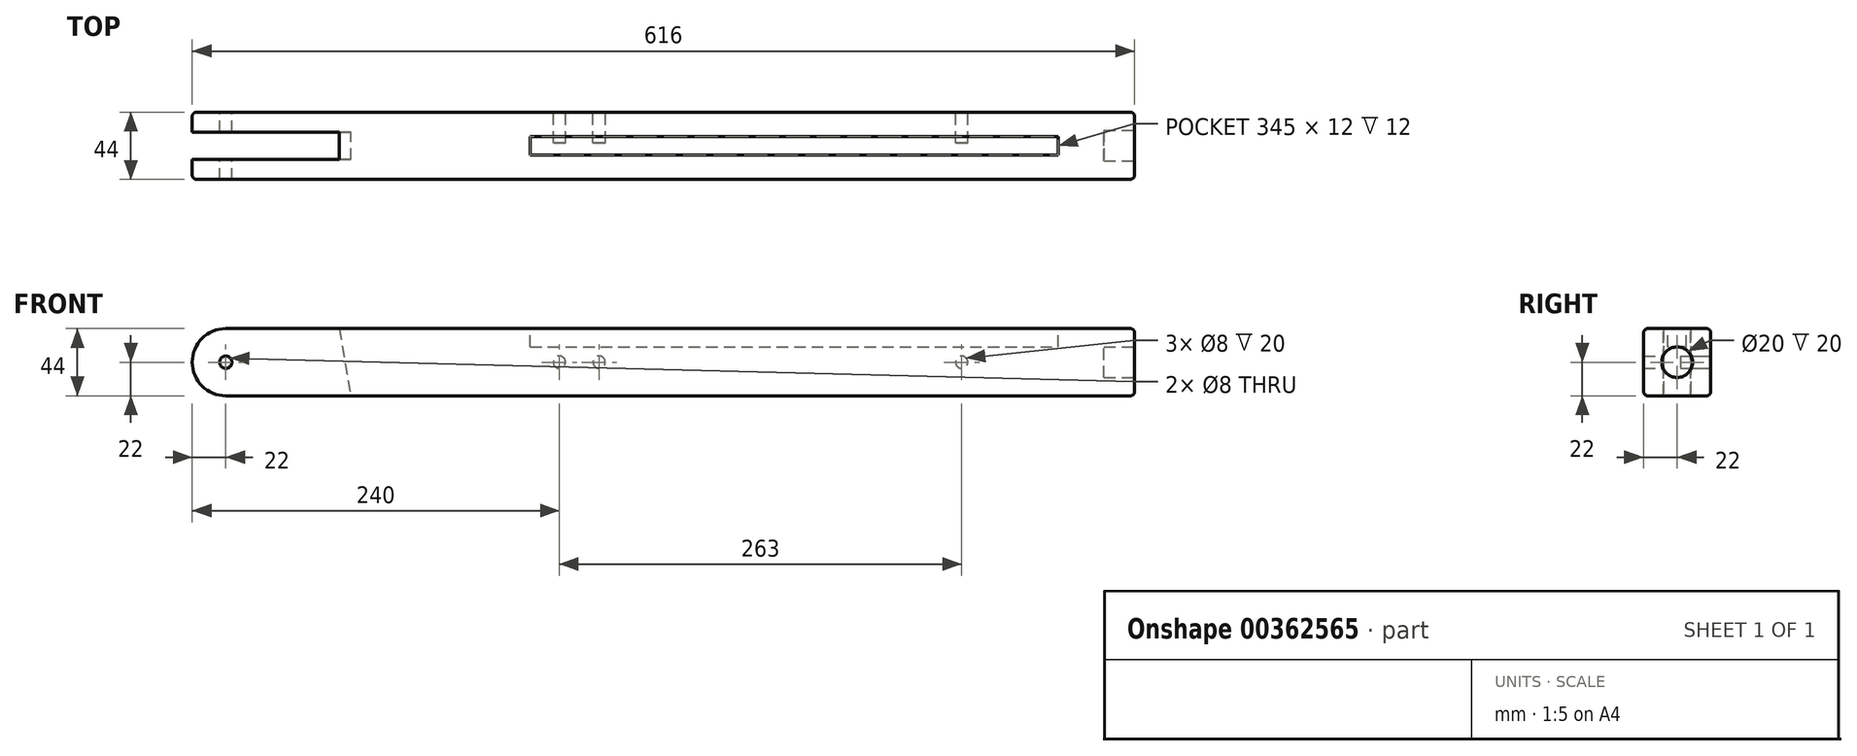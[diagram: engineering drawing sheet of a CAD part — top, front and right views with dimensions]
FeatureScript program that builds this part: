
annotation { "Feature Type Name" : "Feature", "Feature Type Description" : "" }
export const myFeature = defineFeature(function(context is Context, id is Id, definition is map)
    precondition{}
    {
        {
            var Q0;
            Q0=qCreatedBy(makeId("Front.planeOp"),FACE);
            var sketch = newSketch(context, id + "F0", { "sketchPlane" : qUnion([Q0])});
            skArc(sketch, "E0", {"start": v(0, 822) * mm, "mid": v(-22, 800) * mm, "end": v(0, 778) * mm});
            skLineSegment(sketch, "E1", {"start": v(0, 800) * mm, "end": v(594, 800) * mm, "construction": true});
            skLineSegment(sketch, "E2", {"start": v(0, 822) * mm, "end": v(594, 822) * mm});
            skLineSegment(sketch, "E3", {"start": v(594, 778) * mm, "end": v(0, 778) * mm});
            skLineSegment(sketch, "E4", {"start": v(594, 822) * mm, "end": v(594, 778) * mm});
            skLineSegment(sketch, "E5", {"start": v(0, 800) * mm, "end": v(-22, 800) * mm, "construction": true});
            skSolve(sketch);
        }
        {
            var Q0;
            Q0=makeQuery(id+"F0.imprint","IMPRINT",FACE,{"disambiguationData":[TD([[makeQuery(id+"F0.imprint","IMPRINT",EDGE,{"derivedFrom":sQuery(id+"F0.wireOp",EDGE,"E0")}),1.0]])]});
            extrude(context, id + "F1", {"entities" : qUnion([Q0]), "depth" : 44 * mm});
        }
        {
            var Q0;
            Q0=makeQuery(id+"F1.opExtrude","CAP_FACE",FACE,{"disambiguationData":[OSD([sQuery(id+"F0.wireOp",EDGE,"E0"),sQuery(id+"F0.wireOp",EDGE,"E2"),sQuery(id+"F0.wireOp",EDGE,"E3"),sQuery(id+"F0.wireOp",EDGE,"E4")])],"isStart":true});
            cPlane(context, id + "F2", {"entities" : qUnion([Q0]), "cplaneType" : CPlaneType.OFFSET, "offset" : 13 * mm, "oppositeDirection" : true, "width" : 150 * mm, "height" : 150 * mm});
        }
        {
            var Q0;
            Q0=qCreatedBy(id+"F2.planeOp",FACE);
            var sketch = newSketch(context, id + "F3", { "sketchPlane" : qUnion([Q0])});
            skLineSegment(sketch, "E6", {"start": v(22, 778) * mm, "end": v(22, 822) * mm});
            skLineSegment(sketch, "E7", {"start": v(22, 822) * mm, "end": v(-74, 822) * mm});
            skLineSegment(sketch, "E8", {"start": v(-74, 822) * mm, "end": v(-81.76, 778) * mm});
            skLineSegment(sketch, "E9", {"start": v(-81.76, 778) * mm, "end": v(22, 778) * mm});
            skLineSegment(sketch, "E10", {"start": v(22, 800) * mm, "end": v(-77.88, 800) * mm, "construction": true});
            skSolve(sketch);
        }
        {
            var Q0;
            Q0=makeQuery(id+"F3.imprint","IMPRINT",FACE,{"disambiguationData":[TD([[makeQuery(id+"F3.imprint","IMPRINT",EDGE,{"derivedFrom":sQuery(id+"F3.wireOp",EDGE,"E6")}),1.0]])]});
            extrude(context, id + "F4", {"entities" : qUnion([Q0]), "operationType" : NewBodyOperationType.REMOVE, "oppositeDirection" : true, "depth" : 18 * mm});
        }
        {
            var Q0;
            Q0=makeQuery(id+"F1.opExtrude","CAP_FACE",FACE,{"disambiguationData":[OSD([sQuery(id+"F0.wireOp",EDGE,"E0"),sQuery(id+"F0.wireOp",EDGE,"E2"),sQuery(id+"F0.wireOp",EDGE,"E3"),sQuery(id+"F0.wireOp",EDGE,"E4")])],"isStart":true});
            var sketch = newSketch(context, id + "F5", { "sketchPlane" : qUnion([Q0])});
            skCircle(sketch, "E11", {"center": v(0, 800) * mm, "radius": 4 * mm});
            skLineSegment(sketch, "E12", {"start": v(22, 800) * mm, "end": v(-594, 800) * mm, "construction": true});
            skCircle(sketch, "E13", {"center": v(-481, 800) * mm, "radius": 4 * mm});
            skCircle(sketch, "E14", {"center": v(-244, 800) * mm, "radius": 4 * mm});
            skCircle(sketch, "E15", {"center": v(-218, 800) * mm, "radius": 4 * mm});
            skSolve(sketch);
        }
        {
            var Q0;
            Q0=makeQuery(id+"F5.imprint","IMPRINT",FACE,{"disambiguationData":[TD([[makeQuery(id+"F5.imprint","IMPRINT",EDGE,{"derivedFrom":sQuery(id+"F5.wireOp",EDGE,"E11")}),1.0]])]});
            extrude(context, id + "F6", {"entities" : qUnion([Q0]), "operationType" : NewBodyOperationType.REMOVE, "endBound" : BoundingType.THROUGH_ALL, "oppositeDirection" : true, "depth" : 25 * mm});
        }
        {
            var Q0;
            Q0=makeQuery(id+"F5.imprint","IMPRINT",FACE,{"disambiguationData":[TD([[makeQuery(id+"F5.imprint","IMPRINT",EDGE,{"derivedFrom":sQuery(id+"F5.wireOp",EDGE,"E15")}),1.0]])]});
            var Q1;
            Q1=makeQuery(id+"F5.imprint","IMPRINT",FACE,{"disambiguationData":[TD([[makeQuery(id+"F5.imprint","IMPRINT",EDGE,{"derivedFrom":sQuery(id+"F5.wireOp",EDGE,"E14")}),1.0]])]});
            var Q2;
            Q2=makeQuery(id+"F5.imprint","IMPRINT",FACE,{"disambiguationData":[TD([[makeQuery(id+"F5.imprint","IMPRINT",EDGE,{"derivedFrom":sQuery(id+"F5.wireOp",EDGE,"E13")}),1.0]])]});
            extrude(context, id + "F7", {"entities" : qUnion([Q0, Q1, Q2]), "operationType" : NewBodyOperationType.REMOVE, "oppositeDirection" : true, "depth" : 20 * mm});
        }
        {
            var Q0;
            Q0=makeQuery(id+"F1.opExtrude","SWEPT_FACE",FACE,{"disambiguationData":[OSD([sQuery(id+"F0.wireOp",EDGE,"E4")])]});
            var sketch = newSketch(context, id + "F8", { "sketchPlane" : qUnion([Q0])});
            skLineSegment(sketch, "E16", {"start": v(0, 800) * mm, "end": v(-44, 800) * mm, "construction": true});
            skLineSegment(sketch, "E17", {"start": v(-22, 778) * mm, "end": v(-22, 822) * mm, "construction": true});
            skCircle(sketch, "E18", {"center": v(-22, 800) * mm, "radius": 10 * mm});
            skSolve(sketch);
        }
        {
            var Q0;
            Q0=qSketchRegion(id+"F8",true);
            extrude(context, id + "F9", {"entities" : qUnion([Q0]), "operationType" : NewBodyOperationType.REMOVE, "oppositeDirection" : true, "depth" : 20 * mm});
        }
        {
            var Q0;
            Q0=makeQuery(id+"F1.opExtrude","CAP_EDGE",EDGE,{"disambiguationData":[OSD([sQuery(id+"F0.wireOp",EDGE,"E2")])],"isStart":false});
            var Q1;
            Q1=makeQuery(id+"F1.opExtrude","CAP_EDGE",EDGE,{"disambiguationData":[OSD([sQuery(id+"F0.wireOp",EDGE,"E2")])],"isStart":true});
            var Q2;
            Q2=makeQuery(id+"F1.opExtrude","CAP_EDGE",EDGE,{"disambiguationData":[OSD([sQuery(id+"F0.wireOp",EDGE,"E4")])],"isStart":true});
            var Q3;
            Q3=makeQuery(id+"F1.opExtrude","SWEPT_EDGE",EDGE,{"disambiguationData":[OSD([sQuery(id+"F0.wireOp",EDGE,"E2"),sQuery(id+"F0.wireOp",EDGE,"E4")])]});
            var Q4;
            Q4=makeQuery(id+"F1.opExtrude","CAP_EDGE",EDGE,{"disambiguationData":[OSD([sQuery(id+"F0.wireOp",EDGE,"E4")])],"isStart":false});
            var Q5;
            Q5=makeQuery(id+"F1.opExtrude","SWEPT_EDGE",EDGE,{"disambiguationData":[OSD([sQuery(id+"F0.wireOp",EDGE,"E3"),sQuery(id+"F0.wireOp",EDGE,"E4")])]});
            fillet(context, id + "F10", {"entities" : qUnion([Q0, Q1, Q2, Q3, Q4, Q5]), "radius" : 3 * mm, "tangentPropagation" : true, "allowEdgeOverflow" : false});
        }
        {
            var Q0;
            Q0=makeQuery(id+"F1.opExtrude","SWEPT_FACE",FACE,{"disambiguationData":[OSD([sQuery(id+"F0.wireOp",EDGE,"E2")])]});
            var sketch = newSketch(context, id + "F11", { "sketchPlane" : qUnion([Q0])});
            skLineSegment(sketch, "E19", {"start": v(591, -22) * mm, "end": v(74, -22) * mm, "construction": true});
            skLineSegment(sketch, "E20.bottom", {"start": v(199, -16) * mm, "end": v(544, -16) * mm});
            skLineSegment(sketch, "E20.top", {"start": v(199, -28) * mm, "end": v(544, -28) * mm});
            skLineSegment(sketch, "E20.left", {"start": v(199, -16) * mm, "end": v(199, -28) * mm});
            skLineSegment(sketch, "E20.right", {"start": v(544, -16) * mm, "end": v(544, -28) * mm});
            skSolve(sketch);
        }
        {
            var Q0;
            Q0=makeQuery(id+"F11.imprint","IMPRINT",FACE,{"disambiguationData":[TD([[makeQuery(id+"F11.imprint","IMPRINT",EDGE,{"derivedFrom":sQuery(id+"F11.wireOp",EDGE,"E20.bottom")}),-1.0]])]});
            extrude(context, id + "F12", {"entities" : qUnion([Q0]), "operationType" : NewBodyOperationType.REMOVE, "oppositeDirection" : true, "depth" : 12 * mm});
        }
    });
